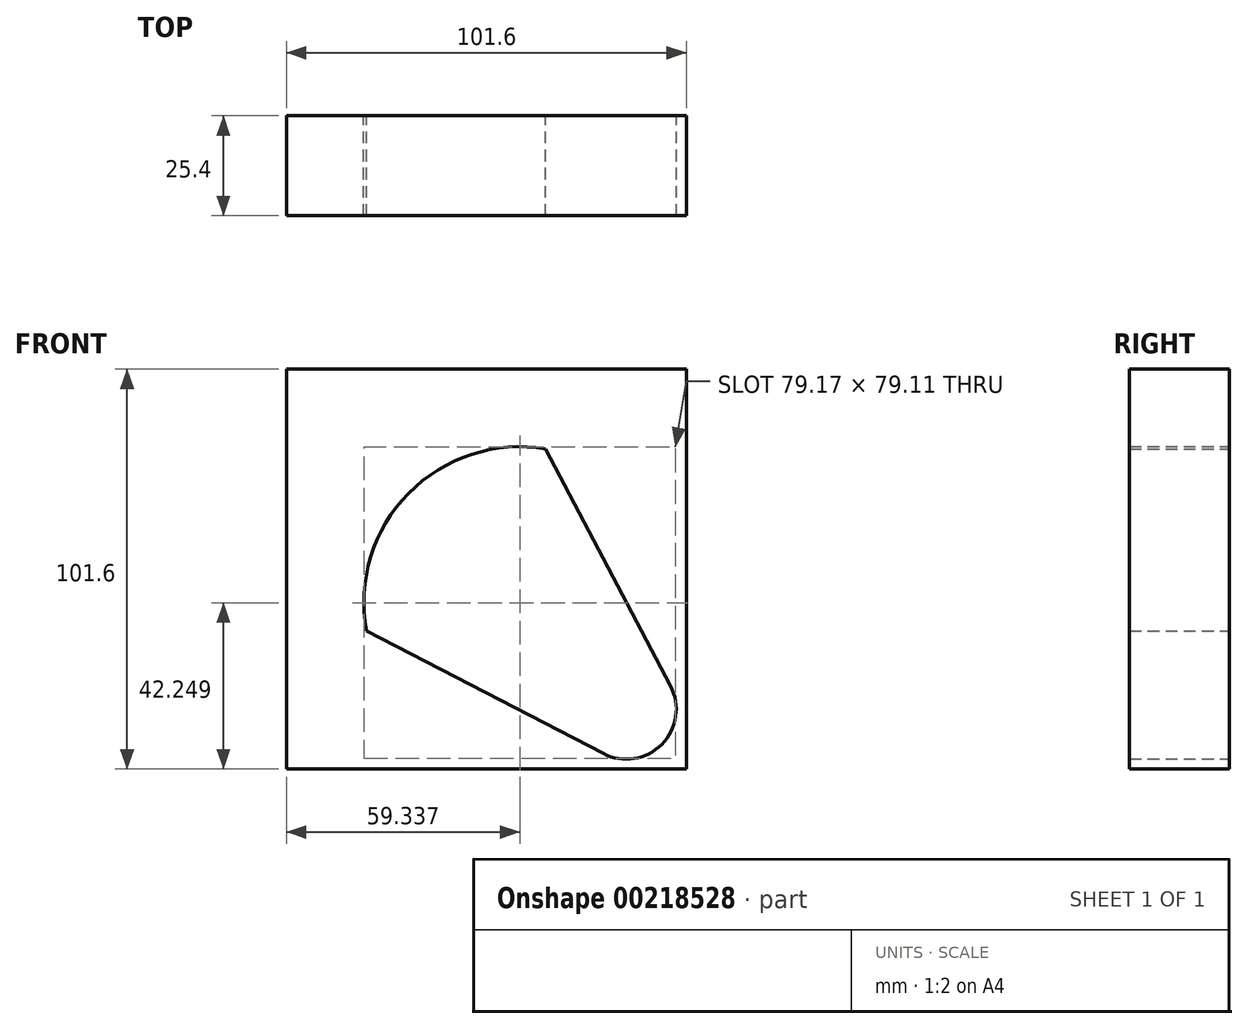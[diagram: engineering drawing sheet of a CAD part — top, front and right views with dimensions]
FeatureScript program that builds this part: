
annotation { "Feature Type Name" : "Feature", "Feature Type Description" : "" }
export const myFeature = defineFeature(function(context is Context, id is Id, definition is map)
    precondition{}
    {
        {
            var Q0;
            Q0=qCreatedBy(makeId("Front.planeOp"),FACE);
            var sketch = newSketch(context, id + "F0", { "sketchPlane" : qUnion([Q0])});
            skLineSegment(sketch, "E0.bottom", {"start": v(-50.8, 50.8) * mm, "end": v(50.8, 50.8) * mm});
            skLineSegment(sketch, "E0.top", {"start": v(-50.8, -50.8) * mm, "end": v(50.8, -50.8) * mm});
            skLineSegment(sketch, "E0.left", {"start": v(-50.8, 50.8) * mm, "end": v(-50.8, -50.8) * mm});
            skLineSegment(sketch, "E0.right", {"start": v(50.8, 50.8) * mm, "end": v(50.8, -50.8) * mm});
            skArc(sketch, "E1", {"start": v(29.72, -46.84) * mm, "mid": v(44.57, -44.5) * mm, "end": v(46.8, -29.64) * mm});
            skPoint(sketch, "E2", {"position": v(-20.57, 20.57) * mm});
            skPoint(sketch, "E3.endSnap0", {"position": v(0, 50.8) * mm});
            skLineSegment(sketch, "E4", {"start": v(-30.47, -15.7) * mm, "end": v(29.72, -46.84) * mm});
            skLineSegment(sketch, "E5", {"start": v(16.87, 27.2) * mm, "end": v(46.8, -29.64) * mm});
            skArc(sketch, "E6", {"start": v(-3.49, 29.22) * mm, "mid": v(-3.56, 29.2) * mm, "end": v(-3.64, 29.19) * mm});
            skPoint(sketch, "E3.end.orphan", {"position": v(4.44, 50.8) * mm});
            skPoint(sketch, "E7.end.orphan", {"position": v(35.56, -48.26) * mm});
            skPoint(sketch, "E8.orphan", {"position": v(32.47, -48.26) * mm});
            skPoint(sketch, "E9.center.orphan", {"position": v(8.57, -8.57) * mm});
            skArc(sketch, "E10", {"start": v(15.09, 30.58) * mm, "mid": v(-19.7, 19.27) * mm, "end": v(-30.47, -15.7) * mm});
            skLineSegment(sketch, "E11", {"start": v(16.87, 27.2) * mm, "end": v(15.09, 30.58) * mm});
            skSolve(sketch);
        }
        {
            var Q0;
            Q0=qSketchRegion(id+"F0",true);
            extrude(context, id + "F1", {"entities" : qUnion([Q0]), "depth" : 25.4 * mm});
        }
    });
